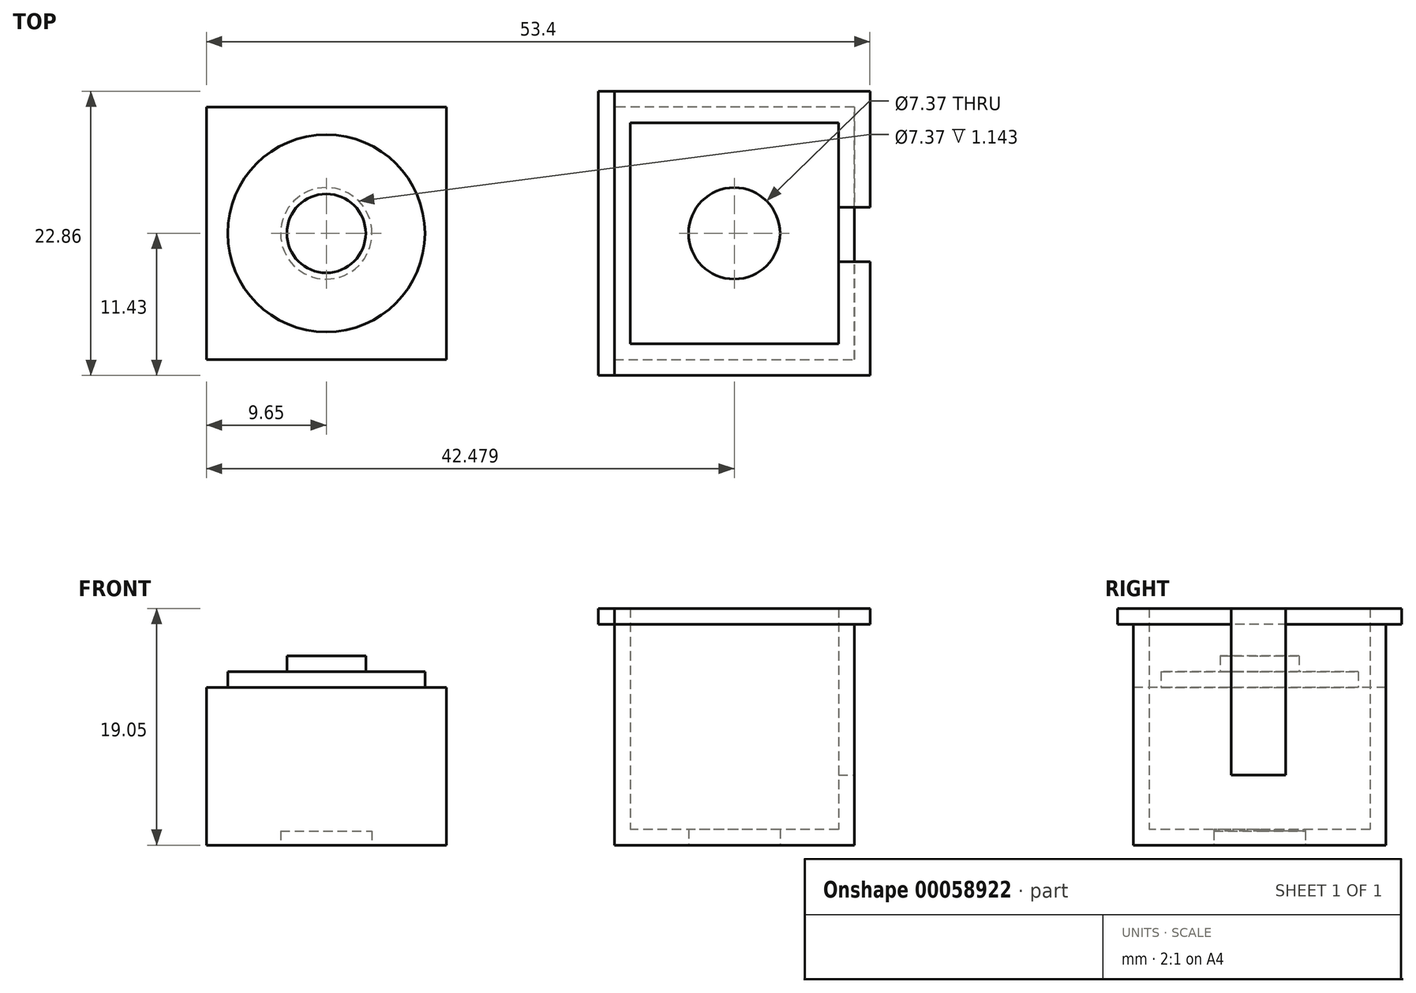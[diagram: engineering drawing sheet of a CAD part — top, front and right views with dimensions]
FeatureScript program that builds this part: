
annotation { "Feature Type Name" : "Feature", "Feature Type Description" : "" }
export const myFeature = defineFeature(function(context is Context, id is Id, definition is map)
    precondition{}
    {
        {
            var Q0;
            Q0=qCreatedBy(makeId("Top.planeOp"),FACE);
            var sketch = newSketch(context, id + "F0", { "sketchPlane" : qUnion([Q0])});
            skLineSegment(sketch, "E0.rect.bottom", {"start": v(-9.65, 10.16) * mm, "end": v(9.65, 10.16) * mm});
            skLineSegment(sketch, "E0.rect.top", {"start": v(-9.65, -10.16) * mm, "end": v(9.65, -10.16) * mm});
            skLineSegment(sketch, "E0.rect.left", {"start": v(-9.65, 10.16) * mm, "end": v(-9.65, -10.16) * mm});
            skLineSegment(sketch, "E0.rect.right", {"start": v(9.65, 10.16) * mm, "end": v(9.65, -10.16) * mm});
            skPoint(sketch, "E0.rect.middle", {"position": v(0, 0) * mm});
            skSolve(sketch);
        }
        {
            var Q0;
            Q0=makeQuery(id+"F0.imprint","IMPRINT",FACE,{"disambiguationData":[TD([[makeQuery(id+"F0.imprint","IMPRINT",EDGE,{"derivedFrom":sQuery(id+"F0.wireOp",EDGE,"E0.rect.bottom")}),-1.0]])]});
            extrude(context, id + "F1", {"entities" : qUnion([Q0]), "depth" : 12.7 * mm});
        }
        {
            var Q0;
            Q0=makeQuery(id+"F1.opExtrude","CAP_FACE",FACE,{"disambiguationData":[OSD([sQuery(id+"F0.wireOp",EDGE,"E0.rect.bottom"),sQuery(id+"F0.wireOp",EDGE,"E0.rect.top"),sQuery(id+"F0.wireOp",EDGE,"E0.rect.left"),sQuery(id+"F0.wireOp",EDGE,"E0.rect.right")])],"isStart":false});
            var sketch = newSketch(context, id + "F2", { "sketchPlane" : qUnion([Q0])});
            skCircle(sketch, "E1", {"center": v(0, 0) * mm, "radius": 7.94 * mm});
            skSolve(sketch);
        }
        {
            var Q0;
            Q0=makeQuery(id+"F2.imprint","IMPRINT",FACE,{"disambiguationData":[TD([[makeQuery(id+"F2.imprint","IMPRINT",EDGE,{"derivedFrom":sQuery(id+"F2.wireOp",EDGE,"E1")}),1.0]])]});
            extrude(context, id + "F3", {"entities" : qUnion([Q0]), "operationType" : NewBodyOperationType.ADD, "depth" : 1.27 * mm});
        }
        {
            var Q0;
            Q0=makeQuery(id+"F3.opExtrude","CAP_FACE",FACE,{"disambiguationData":[OSD([sQuery(id+"F2.wireOp",EDGE,"E1")])],"isStart":false});
            var sketch = newSketch(context, id + "F4", { "sketchPlane" : qUnion([Q0])});
            skCircle(sketch, "E2", {"center": v(0, 0) * mm, "radius": 3.18 * mm});
            skSolve(sketch);
        }
        {
            var Q0;
            Q0=makeQuery(id+"F4.imprint","IMPRINT",FACE,{"disambiguationData":[TD([[makeQuery(id+"F4.imprint","IMPRINT",EDGE,{"derivedFrom":sQuery(id+"F4.wireOp",EDGE,"E2")}),1.0]])]});
            extrude(context, id + "F5", {"entities" : qUnion([Q0]), "operationType" : NewBodyOperationType.ADD, "depth" : 1.27 * mm});
        }
        {
            var Q0;
            Q0=makeQuery(id+"F1.opExtrude","CAP_FACE",FACE,{"disambiguationData":[OSD([sQuery(id+"F0.wireOp",EDGE,"E0.rect.bottom"),sQuery(id+"F0.wireOp",EDGE,"E0.rect.top"),sQuery(id+"F0.wireOp",EDGE,"E0.rect.left"),sQuery(id+"F0.wireOp",EDGE,"E0.rect.right")])],"isStart":true});
            var sketch = newSketch(context, id + "F6", { "sketchPlane" : qUnion([Q0])});
            skCircle(sketch, "E3", {"center": v(0, 0) * mm, "radius": 3.68 * mm});
            skSolve(sketch);
        }
        {
            var Q0;
            Q0=makeQuery(id+"F6.imprint","IMPRINT",FACE,{"disambiguationData":[TD([[makeQuery(id+"F6.imprint","IMPRINT",EDGE,{"derivedFrom":sQuery(id+"F6.wireOp",EDGE,"E3")}),1.0]])]});
            extrude(context, id + "F7", {"entities" : qUnion([Q0]), "operationType" : NewBodyOperationType.REMOVE, "oppositeDirection" : true, "depth" : 1.14 * mm});
        }
        {
            var Q0;
            Q0=qCreatedBy(makeId("Top.planeOp"),FACE);
            var sketch = newSketch(context, id + "F8", { "sketchPlane" : qUnion([Q0])});
            skLineSegment(sketch, "E4.rect.bottom", {"start": v(42.48, 10.16) * mm, "end": v(23.18, 10.16) * mm});
            skLineSegment(sketch, "E4.rect.top", {"start": v(42.48, -10.16) * mm, "end": v(23.18, -10.16) * mm});
            skLineSegment(sketch, "E4.rect.left", {"start": v(42.48, 10.16) * mm, "end": v(42.48, -10.16) * mm});
            skLineSegment(sketch, "E4.rect.right", {"start": v(23.18, 10.16) * mm, "end": v(23.18, -10.16) * mm});
            skPoint(sketch, "E4.rect.middle", {"position": v(32.83, 0) * mm});
            skSolve(sketch);
        }
        {
            var Q0;
            Q0=makeQuery(id+"F8.imprint","IMPRINT",FACE,{"disambiguationData":[TD([[makeQuery(id+"F8.imprint","IMPRINT",EDGE,{"derivedFrom":sQuery(id+"F8.wireOp",EDGE,"E4.rect.bottom")}),1.0]])]});
            extrude(context, id + "F9", {"entities" : qUnion([Q0]), "depth" : 19.05 * mm});
        }
        {
            var Q0;
            Q0=makeQuery(id+"F9.opExtrude","CAP_FACE",FACE,{"disambiguationData":[OSD([sQuery(id+"F8.wireOp",EDGE,"E4.rect.bottom"),sQuery(id+"F8.wireOp",EDGE,"E4.rect.top"),sQuery(id+"F8.wireOp",EDGE,"E4.rect.left"),sQuery(id+"F8.wireOp",EDGE,"E4.rect.right")])],"isStart":false});
            shell(context, id + "F10", {"entities" : qUnion([Q0]), "thickness" : 1.27 * mm});
        }
        {
            var Q0;
            Q0=makeQuery(id+"F9.opExtrude","SWEPT_FACE",FACE,{"disambiguationData":[OSD([sQuery(id+"F8.wireOp",EDGE,"E4.rect.left")])]});
            var sketch = newSketch(context, id + "F11", { "sketchPlane" : qUnion([Q0])});
            skLineSegment(sketch, "E5.bottom", {"start": v(-2.29, 19.05) * mm, "end": v(2.1, 19.05) * mm});
            skLineSegment(sketch, "E5.top", {"start": v(-2.29, 5.64) * mm, "end": v(2.1, 5.64) * mm});
            skLineSegment(sketch, "E5.left", {"start": v(-2.29, 19.05) * mm, "end": v(-2.29, 5.64) * mm});
            skLineSegment(sketch, "E5.right", {"start": v(2.1, 19.05) * mm, "end": v(2.1, 5.64) * mm});
            skSolve(sketch);
        }
        {
            var Q0;
            Q0=makeQuery(id+"F11.imprint","IMPRINT",FACE,{"disambiguationData":[TD([[makeQuery(id+"F11.imprint","IMPRINT",EDGE,{"derivedFrom":sQuery(id+"F11.wireOp",EDGE,"E5.bottom")}),1.0]])]});
            extrude(context, id + "F12", {"entities" : qUnion([Q0]), "operationType" : NewBodyOperationType.REMOVE, "oppositeDirection" : true, "depth" : 1.78 * mm});
        }
        {
            var Q0;
            Q0=makeQuery(id+"F9.opExtrude","CAP_FACE",FACE,{"disambiguationData":[OSD([sQuery(id+"F8.wireOp",EDGE,"E4.rect.bottom"),sQuery(id+"F8.wireOp",EDGE,"E4.rect.top"),sQuery(id+"F8.wireOp",EDGE,"E4.rect.left"),sQuery(id+"F8.wireOp",EDGE,"E4.rect.right")])],"isStart":true});
            var sketch = newSketch(context, id + "F13", { "sketchPlane" : qUnion([Q0])});
            skCircle(sketch, "E6", {"center": v(32.83, 0) * mm, "radius": 3.68 * mm});
            skSolve(sketch);
        }
        {
            var Q0;
            Q0=makeQuery(id+"F13.imprint","IMPRINT",FACE,{"disambiguationData":[TD([[makeQuery(id+"F13.imprint","IMPRINT",EDGE,{"derivedFrom":sQuery(id+"F13.wireOp",EDGE,"E6")}),1.0]])]});
            extrude(context, id + "F14", {"entities" : qUnion([Q0]), "operationType" : NewBodyOperationType.REMOVE, "oppositeDirection" : true, "depth" : 5.08 * mm});
        }
        {
            var Q0;
            Q0=makeQuery(id+"F9.opExtrude","SWEPT_FACE",FACE,{"disambiguationData":[OSD([sQuery(id+"F8.wireOp",EDGE,"E4.rect.top")])]});
            var sketch = newSketch(context, id + "F15", { "sketchPlane" : qUnion([Q0])});
            skLineSegment(sketch, "E7.bottom", {"start": v(23.18, 19.05) * mm, "end": v(42.48, 19.05) * mm});
            skLineSegment(sketch, "E7.top", {"start": v(23.18, 17.78) * mm, "end": v(42.48, 17.78) * mm});
            skLineSegment(sketch, "E7.left", {"start": v(23.18, 19.05) * mm, "end": v(23.18, 17.78) * mm});
            skLineSegment(sketch, "E7.right", {"start": v(42.48, 19.05) * mm, "end": v(42.48, 17.78) * mm});
            skSolve(sketch);
        }
        {
            var Q0;
            Q0=makeQuery(id+"F15.imprint","IMPRINT",FACE,{"disambiguationData":[TD([[makeQuery(id+"F15.imprint","IMPRINT",EDGE,{"derivedFrom":sQuery(id+"F15.wireOp",EDGE,"E7.bottom")}),1.0]])]});
            extrude(context, id + "F16", {"entities" : qUnion([Q0]), "operationType" : NewBodyOperationType.ADD, "depth" : 1.27 * mm});
        }
        {
            var Q0;
            Q0=makeQuery(id+"F9.opExtrude","SWEPT_FACE",FACE,{"disambiguationData":[OSD([sQuery(id+"F8.wireOp",EDGE,"E4.rect.bottom")])]});
            var sketch = newSketch(context, id + "F17", { "sketchPlane" : qUnion([Q0])});
            skLineSegment(sketch, "E8.bottom", {"start": v(-42.48, 19.05) * mm, "end": v(-23.18, 19.05) * mm});
            skLineSegment(sketch, "E8.top", {"start": v(-42.48, 17.78) * mm, "end": v(-23.18, 17.78) * mm});
            skLineSegment(sketch, "E8.left", {"start": v(-42.48, 19.05) * mm, "end": v(-42.48, 17.78) * mm});
            skLineSegment(sketch, "E8.right", {"start": v(-23.18, 19.05) * mm, "end": v(-23.18, 17.78) * mm});
            skSolve(sketch);
        }
        {
            var Q0;
            Q0=makeQuery(id+"F17.imprint","IMPRINT",FACE,{"disambiguationData":[TD([[makeQuery(id+"F17.imprint","IMPRINT",EDGE,{"derivedFrom":sQuery(id+"F17.wireOp",EDGE,"E8.bottom")}),-1.0]])]});
            extrude(context, id + "F18", {"entities" : qUnion([Q0]), "operationType" : NewBodyOperationType.ADD, "depth" : 1.27 * mm});
        }
        {
            var Q0;
            Q0=makeQuery(id+"F18.boolean.opBoolean","MERGE",FACE,{"derivedFrom":[makeQuery(id+"F16.boolean.opBoolean","MERGE",FACE,{"derivedFrom":[makeQuery(id+"F9.opExtrude","SWEPT_FACE",FACE,{"disambiguationData":[OSD([sQuery(id+"F8.wireOp",EDGE,"E4.rect.right")])]}),makeQuery(id+"F16.opExtrude","SWEPT_FACE",FACE,{"disambiguationData":[OSD([sQuery(id+"F15.wireOp",EDGE,"E7.left")])]})]}),makeQuery(id+"F18.opExtrude","SWEPT_FACE",FACE,{"disambiguationData":[OSD([sQuery(id+"F17.wireOp",EDGE,"E8.right")])]})]});
            var sketch = newSketch(context, id + "F19", { "sketchPlane" : qUnion([Q0])});
            skLineSegment(sketch, "E9.bottom", {"start": v(-11.43, 19.05) * mm, "end": v(11.43, 19.05) * mm});
            skLineSegment(sketch, "E9.top", {"start": v(-11.43, 17.78) * mm, "end": v(11.43, 17.78) * mm});
            skLineSegment(sketch, "E9.left", {"start": v(-11.43, 19.05) * mm, "end": v(-11.43, 17.78) * mm});
            skLineSegment(sketch, "E9.right", {"start": v(11.43, 19.05) * mm, "end": v(11.43, 17.78) * mm});
            skSolve(sketch);
        }
        {
            var Q0;
            Q0=makeQuery(id+"F19.imprint","IMPRINT",FACE,{"disambiguationData":[TD([[makeQuery(id+"F19.imprint","IMPRINT",EDGE,{"derivedFrom":sQuery(id+"F19.wireOp",EDGE,"E9.bottom")}),-1.0]])]});
            extrude(context, id + "F20", {"entities" : qUnion([Q0]), "depth" : 1.27 * mm});
        }
        {
            var Q0;
            Q0=makeQuery(id+"F18.boolean.opBoolean","MERGE",FACE,{"derivedFrom":[makeQuery(id+"F16.boolean.opBoolean","MERGE",FACE,{"derivedFrom":[makeQuery(id+"F9.opExtrude","SWEPT_FACE",FACE,{"disambiguationData":[OSD([sQuery(id+"F8.wireOp",EDGE,"E4.rect.left")])]}),makeQuery(id+"F16.opExtrude","SWEPT_FACE",FACE,{"disambiguationData":[OSD([sQuery(id+"F15.wireOp",EDGE,"E7.right")])]})]}),makeQuery(id+"F18.opExtrude","SWEPT_FACE",FACE,{"disambiguationData":[OSD([sQuery(id+"F17.wireOp",EDGE,"E8.left")])]})]});
            var sketch = newSketch(context, id + "F21", { "sketchPlane" : qUnion([Q0])});
            skLineSegment(sketch, "E10.bottom", {"start": v(-11.43, 19.05) * mm, "end": v(-2.29, 19.05) * mm});
            skLineSegment(sketch, "E10.top", {"start": v(-11.43, 17.78) * mm, "end": v(-2.29, 17.78) * mm});
            skLineSegment(sketch, "E10.left", {"start": v(-11.43, 19.05) * mm, "end": v(-11.43, 17.78) * mm});
            skLineSegment(sketch, "E10.right", {"start": v(-2.29, 19.05) * mm, "end": v(-2.29, 17.78) * mm});
            skLineSegment(sketch, "E11.bottom", {"start": v(2.1, 19.05) * mm, "end": v(11.43, 19.05) * mm});
            skLineSegment(sketch, "E11.top", {"start": v(2.1, 17.78) * mm, "end": v(11.43, 17.78) * mm});
            skLineSegment(sketch, "E11.left", {"start": v(2.1, 19.05) * mm, "end": v(2.1, 17.78) * mm});
            skLineSegment(sketch, "E11.right", {"start": v(11.43, 19.05) * mm, "end": v(11.43, 17.78) * mm});
            skSolve(sketch);
        }
        {
            var Q0;
            Q0=makeQuery(id+"F21.imprint","IMPRINT",FACE,{"disambiguationData":[TD([[makeQuery(id+"F21.imprint","IMPRINT",EDGE,{"derivedFrom":sQuery(id+"F21.wireOp",EDGE,"E10.bottom")}),1.0]])]});
            var Q1;
            Q1=makeQuery(id+"F21.imprint","IMPRINT",FACE,{"disambiguationData":[TD([[makeQuery(id+"F21.imprint","IMPRINT",EDGE,{"derivedFrom":sQuery(id+"F21.wireOp",EDGE,"E11.bottom")}),1.0]])]});
            extrude(context, id + "F22", {"entities" : qUnion([Q0, Q1]), "operationType" : NewBodyOperationType.ADD, "depth" : 1.27 * mm});
        }
    });
